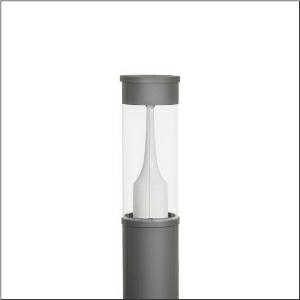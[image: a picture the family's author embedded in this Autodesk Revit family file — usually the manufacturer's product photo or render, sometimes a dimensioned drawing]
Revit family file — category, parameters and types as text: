
# Revit family: city-light_120_iq___p1_0a_5xa5285ff14h_303b
name_source: partatom
category: Lighting Fixtures
units: mm (PartAtom-declared; Revit-internal decimal feet)

## family parameters
Cut with Voids When Loaded = No
Host = Face
Light Source = No
Part Type = Normal
Room Calculation Point = No
Round Connector Dimension = Use Diameter
Shared = No

## types (1)
- --- (1 x LED, 1510 lm, 10.5 W, 3000K)
    Apparent Load = 11 VA
    CIE Flux Codes = 32 61 90 93 100
    Color Rendering = 70
    Color Temperature = 3000K
    Default Elevation = 1800 mm
    Description = City-Light 120 iQ, bollard luminaire, Module 540 iQ-SR, primary light control with 3 zone facetted reflector, of plastic, silver coated, highly specular, structured, primary optical cover: cover, of PMMA, transparent, light distribution: P1.0a, primary light characteristic: strongly asymmetric, LED, High Power LED, rated luminous flux: 1.510lm, luminous efficacy: 144lm/W, light colour: 730, colour temperature: 3000K, control gear: ECG iQ, control: Auto-Match, Temp-Guard, Lumen-Switch, Night-Set, Smart-Wire, Light-Fading, Desk-Remote (wireless, voltage-free reading and setting of iQ features in the workshop via application-optimized NFC function/RFID function), optimised constant luminous flux control (CLO 2.0), Street-Remote, presetting dimming logarithmic, with terminal, 6-pole, max. 2.5mm², mains connection: 220..240V, AC, 50/60Hz, start of lifetime: 11W, end of lifetime: 11W, reduction: 5W, luminaire housing, cylindrical, of extruded aluminium section, coated, Siteco® metallic grey (DB 702S), length: 1.200mm, diameter: 200mm, Module 540 iQ-SR, traffic white (RAL 9016), equipment: standard, protection rating (complete): IP54, insulation class (complete): insulation class II (safety insulation), certification: CE, ENEC, VDE, packaging unit: 1 piece

Light Distribution: P1.0a
    Height = 500 mm
    Lamp = 1 x LED
    Lamp Light Flux = 1510 lm
    Lamp Power = 10.5 W
    Lamp count = 1
    Length = 200 mm  [stored 0.656168 ft]
    Luminous efficacy = 144 lm/W
    Manufacturer = Siteco
    ModVariant = No
    Model = 5XA5285FF14H
    Number of Poles = 1
    OnlyDefault = Yes
    Power Factor = 1
    Product Name = City-Light 120 iQ | P1.0a
    Product group = bollard luminaire | pylon top
    ProductGroupID = 6104
    Protection Class = Protection class II
    Protection Degree = IP 54
    RLX_Detail_Level = 1
    RlxData = <blob elided: 52513 chars, md5=f31f1058>
    Socket = socket
    Standby Power = 0 W
    System Light Flux = 1510 lm
    System Power = 11 W
    Type Comments = factory setting: luminous flux: 100 % | dim-lin: 254 | 419 mA
    Type Image = l_1006922.jpg
    URL = http://relux.com
    VarID = @adj_070841
    Voltage = 0 V
    Weight = 0.00 kg
    Width = 0 mm  [stored 0 ft]

note: [stored X ft] marks values corroborated as IEEE doubles in the binary element streams (Revit-internal decimal feet)

## geometry (parser evidence)
native form markers: Blend x4, Sweep x11
no freeform markers — native parametric forms only
